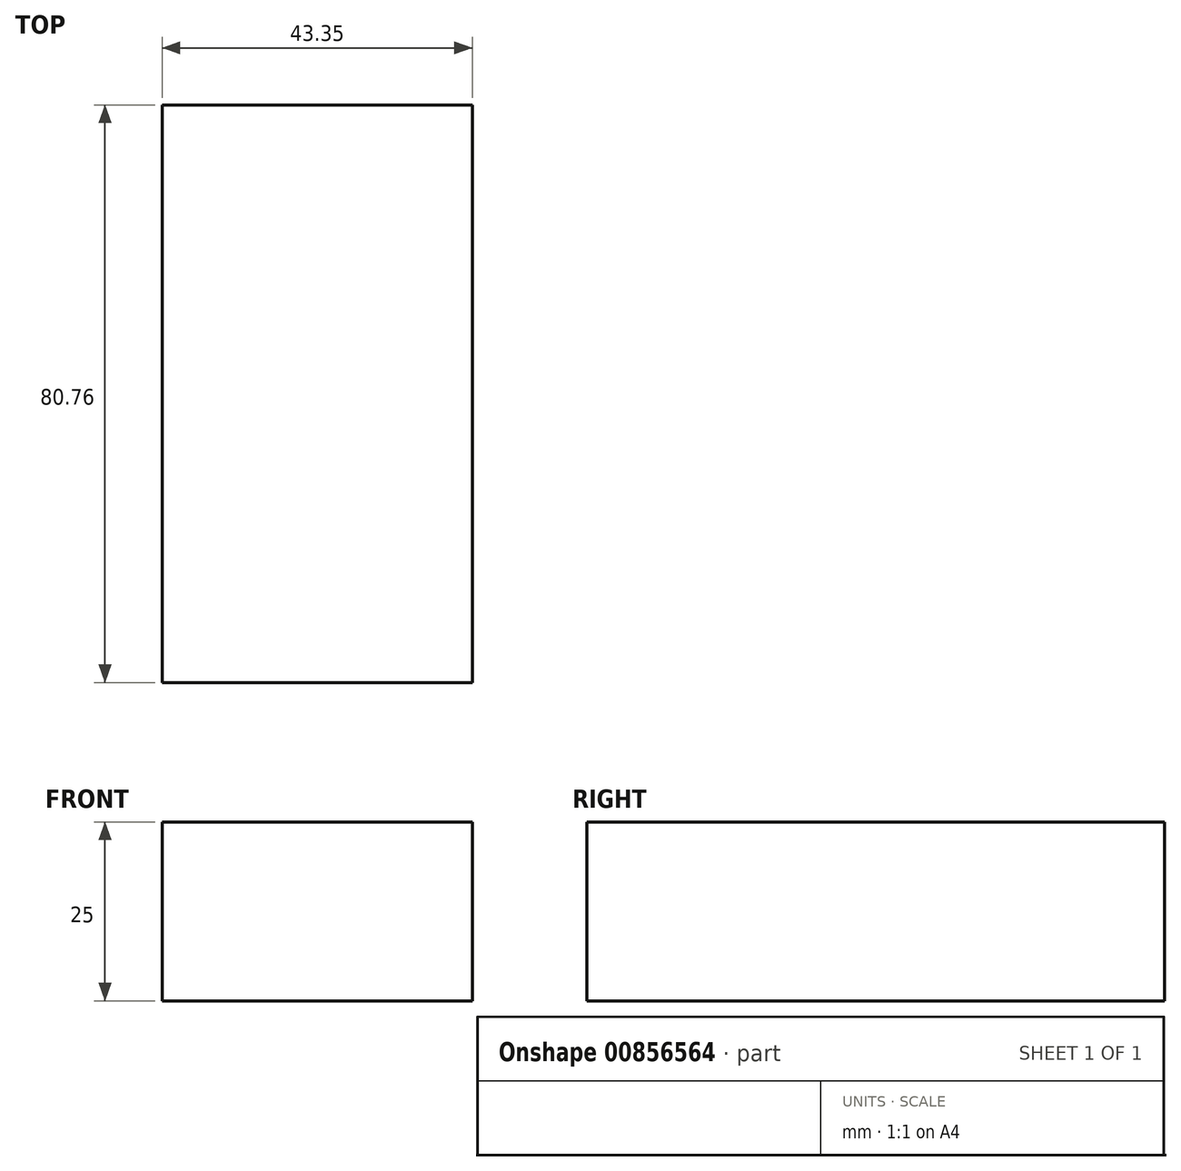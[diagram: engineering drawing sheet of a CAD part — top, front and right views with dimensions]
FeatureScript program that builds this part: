
annotation { "Feature Type Name" : "Feature", "Feature Type Description" : "" }
export const myFeature = defineFeature(function(context is Context, id is Id, definition is map)
    precondition{}
    {
        {
            var Q0;
            Q0=qCreatedBy(makeId("Top.planeOp"),FACE);
            var sketch = newSketch(context, id + "F0", { "sketchPlane" : qUnion([Q0])});
            skLineSegment(sketch, "E0.bottom", {"start": v(-127.46, -42.54) * mm, "end": v(-84.11, -42.54) * mm});
            skLineSegment(sketch, "E0.top", {"start": v(-127.46, 38.22) * mm, "end": v(-84.11, 38.22) * mm});
            skLineSegment(sketch, "E0.left", {"start": v(-127.46, -42.54) * mm, "end": v(-127.46, 38.22) * mm});
            skLineSegment(sketch, "E0.right", {"start": v(-84.11, -42.54) * mm, "end": v(-84.11, 38.22) * mm});
            skSolve(sketch);
        }
        {
            var Q0;
            Q0=makeQuery(id+"F0.imprint","IMPRINT",FACE,{"disambiguationData":[TD([[makeQuery(id+"F0.imprint","IMPRINT",EDGE,{"derivedFrom":sQuery(id+"F0.wireOp",EDGE,"E0.bottom")}),1.0]])]});
            extrude(context, id + "F1", {"entities" : qUnion([Q0]), "depth" : 25 * mm, "offsetDistance" : 25 * mm});
        }
    });
